# Revit family: Skylights_Kalwall_S-line
name_source: partatom
category: Windows
units: mm (PartAtom-declared; Revit-internal decimal feet)

## family parameters
Cut with Voids When Loaded = No
Host = Face
OmniClass Number = 23.30.30.17
OmniClass Title = Metal-Framed Skylights
Room Calculation Point = No
Shared = No

## types (1)
- Default - Please upload Revit family type catalog
    5' module = No
    Default Elevation = 4' - 0"
    Description = Budget-friendly, flat curb S-line skylights are available in 4' and 5' widths and length in 1' increments up to 20'.
    Length = 4' - 1 3/8"
    Manufacturer = Kalwall
    Max Outside Curb Length = 20' - 0"
    Min Outside Curb Length = 4' - 0"
    Model = S-line skylight
    Outside Curb Length = 4' - 0"
    Outside Curb Length Real = 4' - 0"
    Outside Curb Width Real = 4' - 0"
    Panel = 4' Panel Width
    Panel Type Selection = 1
    Product Documentation Link = https://www.kalwall.com
    Product Page URL = https://www.kalwall.com
    Product data url = https://bimobject.com
    Section Length = 4' - 0"
    Section Width = 4' - 0"
    URL = https://www.kalwall.com
    Version = 1
    Width = 4' - 1 3/8"

## geometry (parser evidence)
native form markers: Sweep x9
no freeform markers — native parametric forms only
